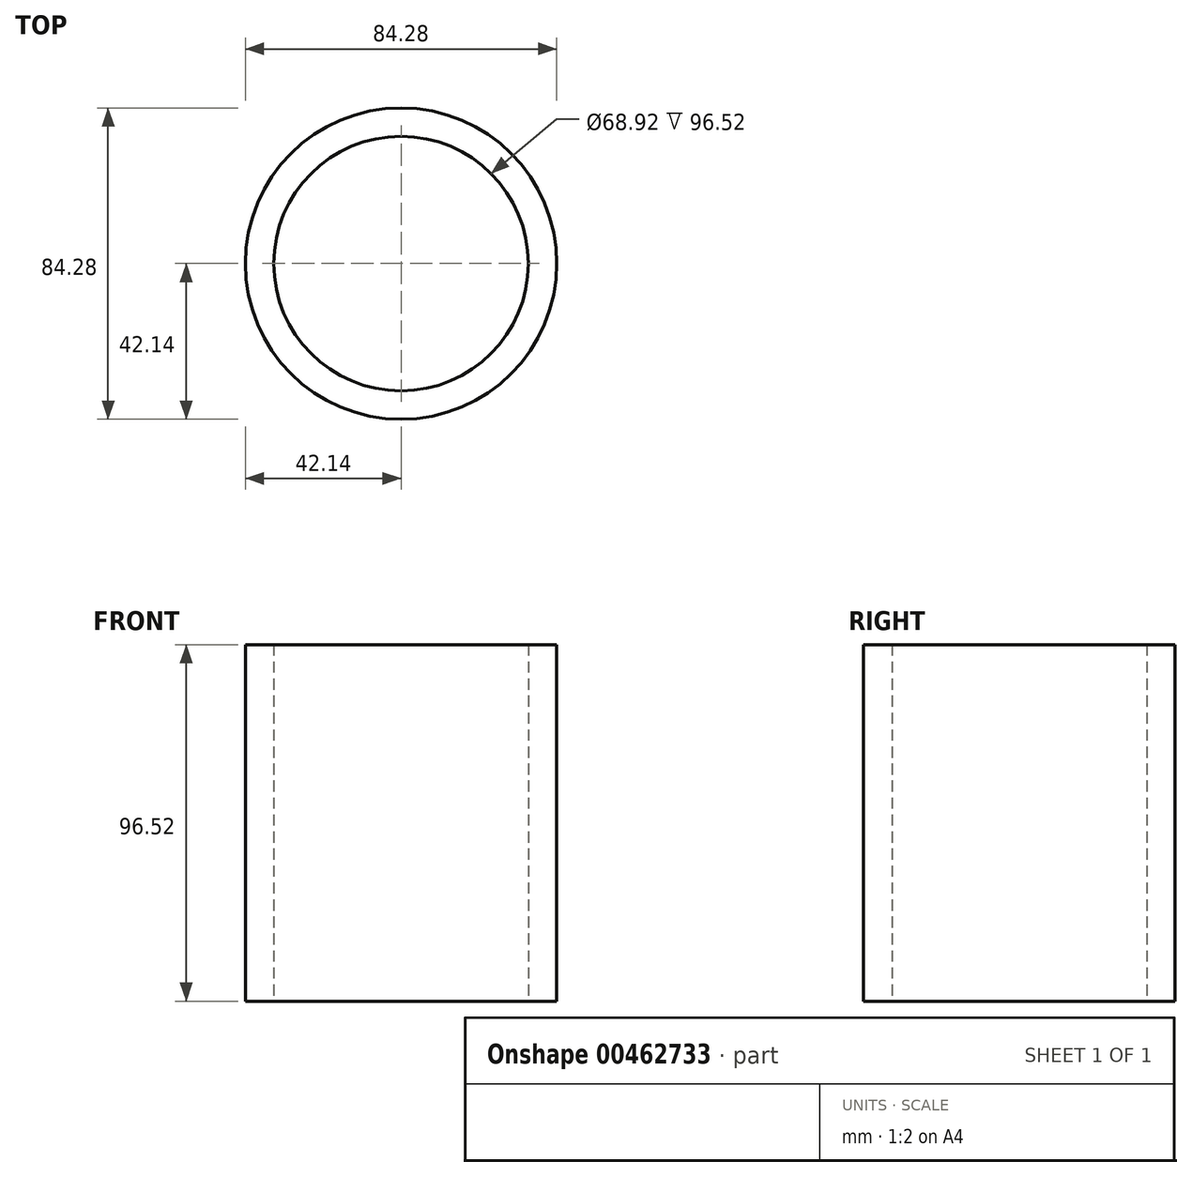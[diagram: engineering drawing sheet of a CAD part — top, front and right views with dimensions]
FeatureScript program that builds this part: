
annotation { "Feature Type Name" : "Feature", "Feature Type Description" : "" }
export const myFeature = defineFeature(function(context is Context, id is Id, definition is map)
    precondition{}
    {
        {
            var Q0;
            Q0=qCreatedBy(makeId("Top.planeOp"),FACE);
            var sketch = newSketch(context, id + "F0", { "sketchPlane" : qUnion([Q0])});
            skCircle(sketch, "E0", {"center": v(0, 0) * mm, "radius": 42.14 * mm});
            skCircle(sketch, "E1", {"center": v(0, 0) * mm, "radius": 34.46 * mm});
            skSolve(sketch);
        }
        {
            var Q0;
            Q0=makeQuery(id+"F0.imprint","IMPRINT",FACE,{"disambiguationData":[TD([[makeQuery(id+"F0.imprint","IMPRINT",EDGE,{"derivedFrom":sQuery(id+"F0.wireOp",EDGE,"E0")}),1.0]])]});
            extrude(context, id + "F1", {"entities" : qUnion([Q0]), "depth" : 96.52 * mm});
        }
    });
